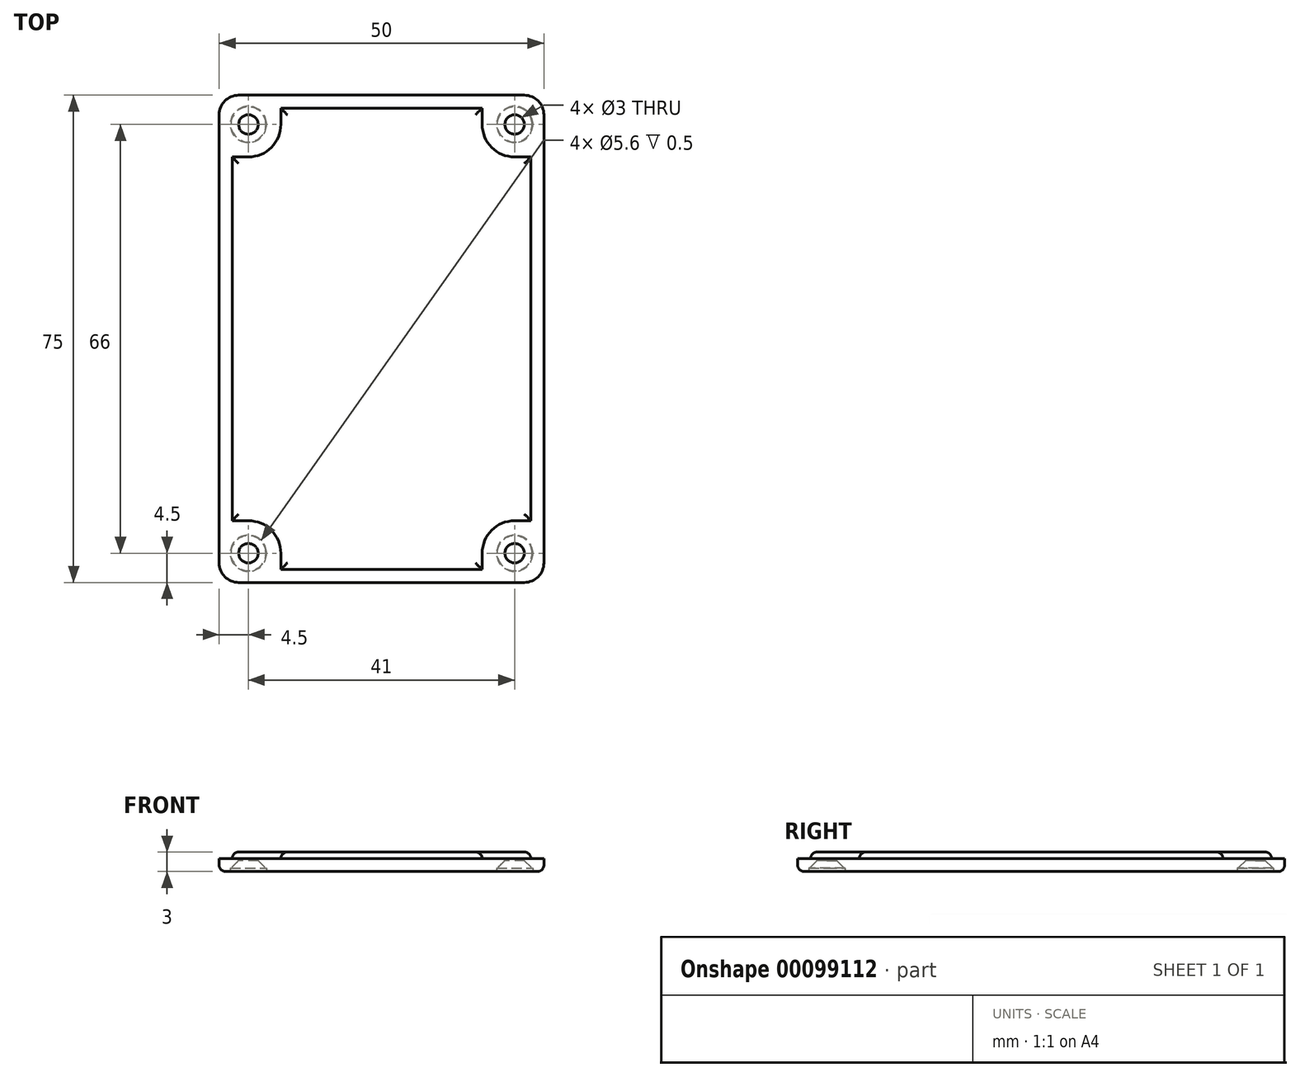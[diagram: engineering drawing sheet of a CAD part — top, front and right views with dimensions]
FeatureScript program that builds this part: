
annotation { "Feature Type Name" : "Feature", "Feature Type Description" : "" }
export const myFeature = defineFeature(function(context is Context, id is Id, definition is map)
    precondition{}
    {
        {
            var Q0;
            Q0=qCreatedBy(makeId("Top.planeOp"),FACE);
            var sketch = newSketch(context, id + "F0", { "sketchPlane" : qUnion([Q0])});
            skLineSegment(sketch, "E0.bottom", {"start": v(3, 0) * mm, "end": v(47, 0) * mm});
            skLineSegment(sketch, "E0.top", {"start": v(3, 75) * mm, "end": v(47, 75) * mm});
            skLineSegment(sketch, "E0.left", {"start": v(0, 3) * mm, "end": v(0, 72) * mm});
            skLineSegment(sketch, "E0.right", {"start": v(50, 3) * mm, "end": v(50, 72) * mm});
            skPoint(sketch, "E1.visualSharp", {"position": v(0, 75) * mm});
            skArc(sketch, "E1.filletArc", {"start": v(3, 75) * mm, "mid": v(0.88, 74.12) * mm, "end": v(0, 72) * mm});
            skPoint(sketch, "E2.visualSharp", {"position": v(50, 75) * mm});
            skArc(sketch, "E2.filletArc", {"start": v(50, 72) * mm, "mid": v(49.12, 74.12) * mm, "end": v(47, 75) * mm});
            skPoint(sketch, "E3.visualSharp", {"position": v(50, 0) * mm});
            skArc(sketch, "E3.filletArc", {"start": v(47, 0) * mm, "mid": v(49.12, 0.88) * mm, "end": v(50, 3) * mm});
            skPoint(sketch, "E4.visualSharp", {"position": v(0, 0) * mm});
            skArc(sketch, "E4.filletArc", {"start": v(0, 3) * mm, "mid": v(0.88, 0.88) * mm, "end": v(3, 0) * mm});
            skSolve(sketch);
        }
        {
            var Q0;
            Q0=makeQuery(id+"F0.imprint","IMPRINT",FACE,{"disambiguationData":[TD([[makeQuery(id+"F0.imprint","IMPRINT",EDGE,{"derivedFrom":sQuery(id+"F0.wireOp",EDGE,"E0.bottom")}),1.0]])]});
            extrude(context, id + "F1", {"entities" : qUnion([Q0]), "depth" : 2 * mm});
        }
        {
            var Q0;
            Q0=makeQuery(id+"F1.opExtrude","CAP_FACE",FACE,{"disambiguationData":[OSD([sQuery(id+"F0.wireOp",EDGE,"E0.bottom"),sQuery(id+"F0.wireOp",EDGE,"E0.top"),sQuery(id+"F0.wireOp",EDGE,"E0.left"),sQuery(id+"F0.wireOp",EDGE,"E0.right"),sQuery(id+"F0.wireOp",EDGE,"E1.filletArc"),sQuery(id+"F0.wireOp",EDGE,"E2.filletArc"),sQuery(id+"F0.wireOp",EDGE,"E3.filletArc"),sQuery(id+"F0.wireOp",EDGE,"E4.filletArc")])],"isStart":false});
            var sketch = newSketch(context, id + "F2", { "sketchPlane" : qUnion([Q0])});
            skCircle(sketch, "E5", {"center": v(4.5, 70.5) * mm, "radius": 1.5 * mm});
            skCircle(sketch, "E6", {"center": v(45.5, 70.5) * mm, "radius": 1.5 * mm});
            skCircle(sketch, "E7", {"center": v(45.5, 4.5) * mm, "radius": 1.5 * mm});
            skCircle(sketch, "E8", {"center": v(4.5, 4.5) * mm, "radius": 1.5 * mm});
            skCircle(sketch, "E9", {"center": v(4.5, 4.5) * mm, "radius": 4.5 * mm, "construction": true});
            skCircle(sketch, "E10", {"center": v(4.5, 70.5) * mm, "radius": 4.5 * mm, "construction": true});
            skCircle(sketch, "E11", {"center": v(45.5, 70.5) * mm, "radius": 4.5 * mm, "construction": true});
            skCircle(sketch, "E12", {"center": v(45.5, 4.5) * mm, "radius": 4.5 * mm, "construction": true});
            skSolve(sketch);
        }
        {
            var Q0;
            Q0=makeQuery(id+"F2.imprint","IMPRINT",FACE,{"disambiguationData":[TD([[makeQuery(id+"F2.imprint","IMPRINT",EDGE,{"derivedFrom":sQuery(id+"F2.wireOp",EDGE,"E5")}),1.0]])]});
            var Q1;
            Q1=makeQuery(id+"F2.imprint","IMPRINT",FACE,{"disambiguationData":[TD([[makeQuery(id+"F2.imprint","IMPRINT",EDGE,{"derivedFrom":sQuery(id+"F2.wireOp",EDGE,"E6")}),1.0]])]});
            var Q2;
            Q2=makeQuery(id+"F2.imprint","IMPRINT",FACE,{"disambiguationData":[TD([[makeQuery(id+"F2.imprint","IMPRINT",EDGE,{"derivedFrom":sQuery(id+"F2.wireOp",EDGE,"E8")}),1.0]])]});
            var Q3;
            Q3=makeQuery(id+"F2.imprint","IMPRINT",FACE,{"disambiguationData":[TD([[makeQuery(id+"F2.imprint","IMPRINT",EDGE,{"derivedFrom":sQuery(id+"F2.wireOp",EDGE,"E7")}),1.0]])]});
            extrude(context, id + "F3", {"entities" : qUnion([Q0, Q1, Q2, Q3]), "operationType" : NewBodyOperationType.REMOVE, "oppositeDirection" : true, "depth" : 5 * mm});
        }
        {
            var Q0;
            Q0=makeQuery(id+"F1.opExtrude","CAP_FACE",FACE,{"disambiguationData":[OSD([sQuery(id+"F0.wireOp",EDGE,"E0.bottom"),sQuery(id+"F0.wireOp",EDGE,"E0.top"),sQuery(id+"F0.wireOp",EDGE,"E0.left"),sQuery(id+"F0.wireOp",EDGE,"E0.right"),sQuery(id+"F0.wireOp",EDGE,"E1.filletArc"),sQuery(id+"F0.wireOp",EDGE,"E2.filletArc"),sQuery(id+"F0.wireOp",EDGE,"E3.filletArc"),sQuery(id+"F0.wireOp",EDGE,"E4.filletArc")])],"isStart":false});
            var sketch = newSketch(context, id + "F4", { "sketchPlane" : qUnion([Q0])});
            skCircle(sketch, "E13", {"center": v(4.5, 4.5) * mm, "radius": 5 * mm});
            skCircle(sketch, "E14", {"center": v(45.5, 4.5) * mm, "radius": 5 * mm});
            skCircle(sketch, "E15", {"center": v(45.5, 70.5) * mm, "radius": 5 * mm});
            skCircle(sketch, "E16", {"center": v(4.5, 70.5) * mm, "radius": 5 * mm});
            skLineSegment(sketch, "E17.bottom", {"start": v(2, 9.5) * mm, "end": v(48, 9.5) * mm});
            skLineSegment(sketch, "E17.top", {"start": v(2, 65.5) * mm, "end": v(48, 65.5) * mm});
            skLineSegment(sketch, "E17.left", {"start": v(2, 9.5) * mm, "end": v(2, 65.5) * mm});
            skLineSegment(sketch, "E17.right", {"start": v(48, 9.5) * mm, "end": v(48, 65.5) * mm});
            skLineSegment(sketch, "E18.bottom", {"start": v(9.5, 2) * mm, "end": v(40.5, 2) * mm});
            skLineSegment(sketch, "E18.top", {"start": v(9.5, 73) * mm, "end": v(40.5, 73) * mm});
            skLineSegment(sketch, "E18.left", {"start": v(9.5, 2) * mm, "end": v(9.5, 73) * mm});
            skLineSegment(sketch, "E18.right", {"start": v(40.5, 2) * mm, "end": v(40.5, 73) * mm});
            skSolve(sketch);
        }
        {
            var Q0;
            Q0=makeQuery(id+"F4.imprint","IMPRINT",FACE,{"disambiguationData":[TD([[makeQuery(id+"F4.imprint","IMPRINT",EDGE,{"derivedFrom":sQuery(id+"F4.wireOp",EDGE,"d846ee22-6f5d-4eb0-8784-35c0200c0626.1")}),1.0]])]});
            var Q1;
            {var subQ5=sQuery(id+"F4.wireOp",EDGE,"E18.bottom");Q1=makeQuery(id+"F4.imprint","IMPRINT",FACE,{"disambiguationData":[TD([[makeQuery(id+"F4.imprint","IMPRINT",EDGE,{"derivedFrom":subQ5}),1.0]])]});}
            var Q2;
            {var subQ5=sQuery(id+"F4.wireOp",EDGE,"E18.top");Q2=makeQuery(id+"F4.imprint","IMPRINT",FACE,{"disambiguationData":[TD([[makeQuery(id+"F4.imprint","IMPRINT",EDGE,{"derivedFrom":subQ5}),-1.0]])]});}
            var Q3;
            {var subQ0=sQuery(id+"F4.wireOp",EDGE,"E17.left");Q3=makeQuery(id+"F4.imprint","IMPRINT",FACE,{"disambiguationData":[TD([[makeQuery(id+"F4.imprint","IMPRINT",EDGE,{"derivedFrom":subQ0}),-1.0]])]});}
            var Q4;
            {var subQ0=sQuery(id+"F4.wireOp",EDGE,"E18.left");var subQ1=sQuery(id+"F4.wireOp",EDGE,"E17.bottom");var subQ2=makeQuery(id+"F4.imprint","INTERSECT",VERTEX,{"derivedFrom":[subQ1,subQ0]});Q4=makeQuery(id+"F4.imprint","IMPRINT",FACE,{"disambiguationData":[TD([[makeQuery(id+"F4.imprint","IMPRINT",EDGE,{"disambiguationData":[TD([[subQ2,-1.0]])],"derivedFrom":subQ1}),1.0]])]});}
            var Q5;
            {var subQ0=sQuery(id+"F4.wireOp",EDGE,"E17.right");Q5=makeQuery(id+"F4.imprint","IMPRINT",FACE,{"disambiguationData":[TD([[makeQuery(id+"F4.imprint","IMPRINT",EDGE,{"derivedFrom":subQ0}),1.0]])]});}
            var Q6;
            {var subQ0=sQuery(id+"F4.wireOp",EDGE,"E18.left");var subQ1=sQuery(id+"F4.wireOp",EDGE,"E16");var subQ2=makeQuery(id+"F4.imprint","INTERSECT",VERTEX,{"derivedFrom":[subQ1,subQ0]});Q6=makeQuery(id+"F4.imprint","IMPRINT",FACE,{"disambiguationData":[TD([[makeQuery(id+"F4.imprint","IMPRINT",EDGE,{"disambiguationData":[TD([[subQ2,1.0]])],"derivedFrom":subQ1}),-1.0]])]});}
            var Q7;
            {var subQ0=sQuery(id+"F4.wireOp",EDGE,"E18.right");var subQ1=sQuery(id+"F4.wireOp",EDGE,"E15");var subQ2=makeQuery(id+"F4.imprint","INTERSECT",VERTEX,{"derivedFrom":[subQ1,subQ0]});Q7=makeQuery(id+"F4.imprint","IMPRINT",FACE,{"disambiguationData":[TD([[makeQuery(id+"F4.imprint","IMPRINT",EDGE,{"disambiguationData":[TD([[subQ2,-1.0]])],"derivedFrom":subQ1}),-1.0]])]});}
            var Q8;
            {var subQ0=sQuery(id+"F4.wireOp",EDGE,"E17.bottom");var subQ1=sQuery(id+"F4.wireOp",EDGE,"E14");var subQ2=makeQuery(id+"F4.imprint","INTERSECT",VERTEX,{"derivedFrom":[subQ1,subQ0]});Q8=makeQuery(id+"F4.imprint","IMPRINT",FACE,{"disambiguationData":[TD([[makeQuery(id+"F4.imprint","IMPRINT",EDGE,{"disambiguationData":[TD([[subQ2,-1.0]])],"derivedFrom":subQ1}),-1.0]])]});}
            var Q9;
            {var subQ0=sQuery(id+"F4.wireOp",EDGE,"E17.bottom");var subQ1=sQuery(id+"F4.wireOp",EDGE,"E13");var subQ2=makeQuery(id+"F4.imprint","INTERSECT",VERTEX,{"derivedFrom":[subQ1,subQ0]});Q9=makeQuery(id+"F4.imprint","IMPRINT",FACE,{"disambiguationData":[TD([[makeQuery(id+"F4.imprint","IMPRINT",EDGE,{"disambiguationData":[TD([[subQ2,1.0]])],"derivedFrom":subQ1}),-1.0]])]});}
            extrude(context, id + "F5", {"entities" : qUnion([Q0, Q1, Q2, Q3, Q4, Q5, Q6, Q7, Q8, Q9]), "operationType" : NewBodyOperationType.ADD, "depth" : 1 * mm});
        }
        {
            var Q0;
            Q0=makeQuery(id+"F5.opExtrude","CAP_FACE",FACE,{"disambiguationData":[OSD([sQuery(id+"F4.wireOp",EDGE,"E17.bottom"),sQuery(id+"F4.wireOp",EDGE,"E17.top"),sQuery(id+"F4.wireOp",EDGE,"E17.left"),sQuery(id+"F4.wireOp",EDGE,"E17.right"),sQuery(id+"F4.wireOp",EDGE,"E18.bottom"),sQuery(id+"F4.wireOp",EDGE,"E18.top"),sQuery(id+"F4.wireOp",EDGE,"E18.left"),sQuery(id+"F4.wireOp",EDGE,"E18.right")])],"isStart":false});
            fillet(context, id + "F6", {"entities" : qUnion([Q0]), "radius" : 1 * mm, "tangentPropagation" : true, "allowEdgeOverflow" : false});
        }
        {
            var Q0;
            Q0=makeQuery(id+"F1.opExtrude","CAP_EDGE",EDGE,{"disambiguationData":[OSD([sQuery(id+"F0.wireOp",EDGE,"E0.left")])],"isStart":true});
            fillet(context, id + "F7", {"entities" : qUnion([Q0]), "radius" : 1 * mm, "tangentPropagation" : true, "allowEdgeOverflow" : false});
        }
        {
            var Q0;
            Q0=makeQuery(id+"F1.opExtrude","CAP_FACE",FACE,{"disambiguationData":[OSD([sQuery(id+"F0.wireOp",EDGE,"E0.bottom"),sQuery(id+"F0.wireOp",EDGE,"E0.top"),sQuery(id+"F0.wireOp",EDGE,"E0.left"),sQuery(id+"F0.wireOp",EDGE,"E0.right"),sQuery(id+"F0.wireOp",EDGE,"E1.filletArc"),sQuery(id+"F0.wireOp",EDGE,"E2.filletArc"),sQuery(id+"F0.wireOp",EDGE,"E3.filletArc"),sQuery(id+"F0.wireOp",EDGE,"E4.filletArc")])],"isStart":true});
            var sketch = newSketch(context, id + "F8", { "sketchPlane" : qUnion([Q0])});
            skCircle(sketch, "E19", {"center": v(4.5, -4.5) * mm, "radius": 2.8 * mm});
            skCircle(sketch, "E20", {"center": v(45.5, -4.5) * mm, "radius": 2.8 * mm});
            skCircle(sketch, "E21", {"center": v(45.5, -70.5) * mm, "radius": 2.8 * mm});
            skCircle(sketch, "E22", {"center": v(4.5, -70.5) * mm, "radius": 2.8 * mm});
            skSolve(sketch);
        }
        {
            var Q0;
            Q0=qSketchRegion(id+"F8",true);
            extrude(context, id + "F9", {"entities" : qUnion([Q0]), "operationType" : NewBodyOperationType.REMOVE, "oppositeDirection" : true, "depth" : .5 * mm});
        }
        {
            var Q0;
            Q0=makeQuery(id+"F9.boolean.opBoolean","INTERSECT",EDGE,{"derivedFrom":[makeQuery(id+"F3.boolean.opBoolean","COPY",FACE,{"derivedFrom":makeQuery(id+"F3.opExtrude","SWEPT_FACE",FACE,{"disambiguationData":[OSD([sQuery(id+"F2.wireOp",EDGE,"E8")])]})}),makeQuery(id+"F9.opExtrude","CAP_FACE",FACE,{"disambiguationData":[OSD([sQuery(id+"F8.wireOp",EDGE,"E19")])],"isStart":false})]});
            var Q1;
            Q1=makeQuery(id+"F9.boolean.opBoolean","INTERSECT",EDGE,{"derivedFrom":[makeQuery(id+"F3.boolean.opBoolean","COPY",FACE,{"derivedFrom":makeQuery(id+"F3.opExtrude","SWEPT_FACE",FACE,{"disambiguationData":[OSD([sQuery(id+"F2.wireOp",EDGE,"E7")])]})}),makeQuery(id+"F9.opExtrude","CAP_FACE",FACE,{"disambiguationData":[OSD([sQuery(id+"F8.wireOp",EDGE,"E20")])],"isStart":false})]});
            var Q2;
            Q2=makeQuery(id+"F9.boolean.opBoolean","INTERSECT",EDGE,{"derivedFrom":[makeQuery(id+"F3.boolean.opBoolean","COPY",FACE,{"derivedFrom":makeQuery(id+"F3.opExtrude","SWEPT_FACE",FACE,{"disambiguationData":[OSD([sQuery(id+"F2.wireOp",EDGE,"E5")])]})}),makeQuery(id+"F9.opExtrude","CAP_FACE",FACE,{"disambiguationData":[OSD([sQuery(id+"F8.wireOp",EDGE,"E22")])],"isStart":false})]});
            var Q3;
            Q3=makeQuery(id+"F9.boolean.opBoolean","INTERSECT",EDGE,{"derivedFrom":[makeQuery(id+"F3.boolean.opBoolean","COPY",FACE,{"derivedFrom":makeQuery(id+"F3.opExtrude","SWEPT_FACE",FACE,{"disambiguationData":[OSD([sQuery(id+"F2.wireOp",EDGE,"E6")])]})}),makeQuery(id+"F9.opExtrude","CAP_FACE",FACE,{"disambiguationData":[OSD([sQuery(id+"F8.wireOp",EDGE,"E21")])],"isStart":false})]});
            chamfer(context, id + "F10", {"entities" : qUnion([Q0, Q1, Q2, Q3]), "chamferType" : ChamferType.OFFSET_ANGLE, "width" : 1.2 * mm, "oppositeDirection" : false, "angle" : 45 * degree, "tangentPropagation" : true});
        }
    });
